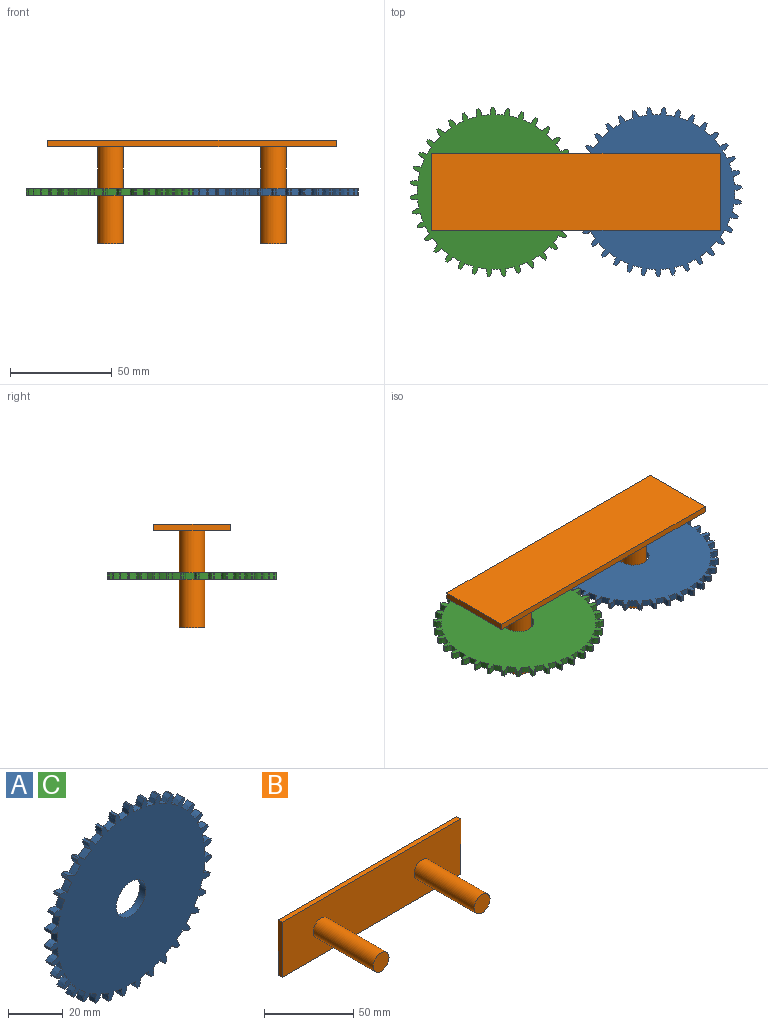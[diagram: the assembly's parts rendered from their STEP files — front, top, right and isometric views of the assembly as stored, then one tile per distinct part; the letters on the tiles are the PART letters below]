
ASSEMBLY  parts=3 mates=2
PART A: 143 faces, bbox 83.3x3.2x83.2 mm
  f0: cylinder r=38.1mm len=4.18mm, axis (0,1,0), area 13.4mm2, adj f1,f139,f140,f141
  f1: extruded ~3.64x3.18mm, area 11.9mm2, adj f0,f2,f140,f141
  f2: plane 3.18x0.92mm, normal (1,0,-0.04), area 2.9mm2, adj f1,f3,f140,f141
  f3: extruded ~3.57x3.18mm, area 11.9mm2, adj f2,f4,f140,f141
  f4: cylinder r=38.1mm len=4.22mm, axis (0,1,0), area 13.4mm2, adj f3,f5,f140,f141
  f5: extruded ~3.46x3.18mm, area 11.9mm2, adj f4,f6,f140,f141
  f6: plane 3.18x0.91mm, normal (0.99,0,0.13), area 2.9mm2, adj f5,f7,f140,f141
  f7: extruded ~3.69x3.18mm, area 11.9mm2, adj f6,f8,f140,f141
  f8: cylinder r=38.1mm len=4.11mm, axis (0,1,0), area 13.4mm2, adj f7,f9,f140,f141
  f9: extruded ~3.18x3.17mm, area 11.9mm2, adj f8,f10,f140,f141
  f10: plane 3.18x0.88mm, normal (0.95,0,0.31), area 2.9mm2, adj f9,f11,f140,f141
  f11: extruded ~3.69x3.18mm, area 11.9mm2, adj f10,f12,f140,f141
  f12: cylinder r=38.1mm len=3.88mm, axis (0,1,0), area 13.4mm2, adj f11,f13,f140,f141
  f13: extruded ~3.18x2.78mm, area 11.9mm2, adj f12,f14,f140,f141
  f14: plane 3.18x0.81mm, normal (0.88,0,0.47), area 2.9mm2, adj f13,f15,f140,f141
  f15: extruded ~3.58x3.18mm, area 11.9mm2, adj f14,f16,f140,f141
  f16: cylinder r=38.1mm len=3.52mm, axis (0,1,0), area 13.4mm2, adj f15,f17,f140,f141
  f17: extruded ~3.18x2.91mm, area 11.9mm2, adj f16,f18,f140,f141
  f18: plane 3.18x0.72mm, normal (0.78,0,0.62), area 2.9mm2, adj f17,f19,f140,f141
  f19: extruded ~3.35x3.18mm, area 11.9mm2, adj f18,f20,f140,f141
  f20: cylinder r=38.1mm len=3.18mm, axis (0,1,0), area 13.4mm2, adj f19,f21,f140,f141
  f21: extruded ~3.28x3.18mm, area 11.9mm2, adj f20,f22,f140,f141
  f22: plane 3.18x0.69mm, normal (0.66,0,0.75), area 2.9mm2, adj f21,f23,f140,f141
  f23: extruded ~3.18x3.01mm, area 11.9mm2, adj f22,f24,f140,f141
  f24: cylinder r=38.1mm len=3.41mm, axis (0,1,0), area 13.4mm2, adj f23,f25,f140,f141
  f25: extruded ~3.53x3.18mm, area 11.9mm2, adj f24,f26,f140,f141
  f26: plane 3.18x0.79mm, normal (0.51,0,0.86), area 2.9mm2, adj f25,f27,f140,f141
  f27: extruded ~3.18x2.66mm, area 11.9mm2, adj f26,f28,f140,f141
  f28: cylinder r=38.1mm len=3.8mm, axis (0,1,0), area 13.4mm2, adj f27,f29,f140,f141
  f29: extruded ~3.68x3.18mm, area 11.9mm2, adj f28,f30,f140,f141
  f30: plane 3.18x0.86mm, normal (0.35,0,0.94), area 2.9mm2, adj f29,f31,f140,f141
  f31: extruded ~3.18x3.08mm, area 11.9mm2, adj f30,f32,f140,f141
  f32: cylinder r=38.1mm len=4.07mm, axis (0,1,0), area 13.4mm2, adj f31,f33,f140,f141
  f33: extruded ~3.7x3.18mm, area 11.9mm2, adj f32,f34,f140,f141
  f34: plane 3.18x0.91mm, normal (0.18,0,0.98), area 2.9mm2, adj f33,f35,f140,f141
  f35: extruded ~3.4x3.18mm, area 11.9mm2, adj f34,f36,f140,f141
  f36: cylinder r=38.1mm len=4.2mm, axis (0,1,0), area 13.4mm2, adj f35,f37,f140,f141
  f37: extruded ~3.61x3.18mm, area 11.9mm2, adj f36,f38,f140,f141
  f38: plane 3.18x0.92mm, normal (0,0,1), area 2.9mm2, adj f37,f39,f140,f141
  f39: extruded ~3.61x3.18mm, area 11.9mm2, adj f38,f40,f140,f141
  f40: cylinder r=38.1mm len=4.2mm, axis (0,1,0), area 13.4mm2, adj f39,f41,f140,f141
  f41: extruded ~3.4x3.18mm, area 11.9mm2, adj f40,f42,f140,f141
  f42: plane 3.18x0.91mm, normal (-0.18,0,0.98), area 2.9mm2, adj f41,f43,f140,f141
  f43: extruded ~3.7x3.18mm, area 11.9mm2, adj f42,f44,f140,f141
  f44: cylinder r=38.1mm len=4.07mm, axis (0,1,0), area 13.4mm2, adj f43,f45,f140,f141
  f45: extruded ~3.18x3.08mm, area 11.9mm2, adj f44,f46,f140,f141
  f46: plane 3.18x0.86mm, normal (-0.35,0,0.94), area 2.9mm2, adj f45,f47,f140,f141
  f47: extruded ~3.68x3.18mm, area 11.9mm2, adj f46,f48,f140,f141
  f48: cylinder r=38.1mm len=3.8mm, axis (0,1,0), area 13.4mm2, adj f47,f49,f140,f141
  f49: extruded ~3.18x2.66mm, area 11.9mm2, adj f48,f50,f140,f141
  f50: plane 3.18x0.79mm, normal (-0.51,0,0.86), area 2.9mm2, adj f49,f51,f140,f141
  f51: extruded ~3.53x3.18mm, area 11.9mm2, adj f50,f52,f140,f141
  f52: cylinder r=38.1mm len=3.41mm, axis (0,1,0), area 13.4mm2, adj f51,f53,f140,f141
  f53: extruded ~3.18x3.01mm, area 11.9mm2, adj f52,f54,f140,f141
  f54: plane 3.18x0.69mm, normal (-0.66,0,0.75), area 2.9mm2, adj f53,f55,f140,f141
  f55: extruded ~3.28x3.18mm, area 11.9mm2, adj f54,f56,f140,f141
  f56: cylinder r=38.1mm len=3.18mm, axis (0,1,0), area 13.4mm2, adj f55,f57,f140,f141
  f57: extruded ~3.35x3.18mm, area 11.9mm2, adj f56,f58,f140,f141
  f58: plane 3.18x0.72mm, normal (-0.78,0,0.62), area 2.9mm2, adj f57,f59,f140,f141
  f59: extruded ~3.18x2.91mm, area 11.9mm2, adj f58,f60,f140,f141
  f60: cylinder r=38.1mm len=3.52mm, axis (0,1,0), area 13.4mm2, adj f59,f61,f140,f141
  f61: extruded ~3.58x3.18mm, area 11.9mm2, adj f60,f62,f140,f141
  f62: plane 3.18x0.81mm, normal (-0.88,0,0.47), area 2.9mm2, adj f61,f63,f140,f141
  f63: extruded ~3.18x2.78mm, area 11.9mm2, adj f62,f64,f140,f141
  f64: cylinder r=38.1mm len=3.88mm, axis (0,1,0), area 13.4mm2, adj f63,f65,f140,f141
  f65: extruded ~3.69x3.18mm, area 11.9mm2, adj f64,f66,f140,f141
  f66: plane 3.18x0.88mm, normal (-0.95,0,0.31), area 2.9mm2, adj f65,f67,f140,f141
  f67: extruded ~3.18x3.17mm, area 11.9mm2, adj f66,f68,f140,f141
  f68: cylinder r=38.1mm len=4.11mm, axis (0,1,0), area 13.4mm2, adj f67,f69,f140,f141
  f69: extruded ~3.69x3.18mm, area 11.9mm2, adj f68,f70,f140,f141
  f70: plane 3.18x0.91mm, normal (-0.99,0,0.13), area 2.9mm2, adj f69,f71,f140,f141
  f71: extruded ~3.46x3.18mm, area 11.9mm2, adj f70,f72,f140,f141
  f72: cylinder r=38.1mm len=4.22mm, axis (0,1,0), area 13.4mm2, adj f71,f73,f140,f141
  f73: extruded ~3.57x3.18mm, area 11.9mm2, adj f72,f74,f140,f141
  f74: plane 3.18x0.92mm, normal (-1,0,-0.04), area 2.9mm2, adj f73,f75,f140,f141
  f75: extruded ~3.64x3.18mm, area 11.9mm2, adj f74,f76,f140,f141
  f76: cylinder r=38.1mm len=4.18mm, axis (0,1,0), area 13.4mm2, adj f75,f77,f140,f141
  f77: extruded ~3.33x3.18mm, area 11.9mm2, adj f76,f78,f140,f141
  f78: plane 3.18x0.9mm, normal (-0.97,0,-0.22), area 2.9mm2, adj f77,f79,f140,f141
  f79: extruded ~3.71x3.18mm, area 11.9mm2, adj f78,f80,f140,f141
  f80: cylinder r=38.1mm len=4.01mm, axis (0,1,0), area 13.4mm2, adj f79,f81,f140,f141
  f81: extruded ~3.18x2.99mm, area 11.9mm2, adj f80,f82,f140,f141
  f82: plane 3.18x0.85mm, normal (-0.92,0,-0.39), area 2.9mm2, adj f81,f83,f140,f141
  f83: extruded ~3.65x3.18mm, area 11.9mm2, adj f82,f84,f140,f141
  f84: cylinder r=38.1mm len=3.72mm, axis (0,1,0), area 13.4mm2, adj f83,f85,f140,f141
  f85: extruded ~3.18x2.7mm, area 11.9mm2, adj f84,f86,f140,f141
  f86: plane 3.18x0.77mm, normal (-0.83,0,-0.55), area 2.9mm2, adj f85,f87,f140,f141
  f87: extruded ~3.48x3.18mm, area 11.9mm2, adj f86,f88,f140,f141
  f88: cylinder r=38.1mm len=3.3mm, axis (0,1,0), area 13.4mm2, adj f87,f89,f140,f141
  f89: extruded ~3.18x3.11mm, area 11.9mm2, adj f88,f90,f140,f141
  f90: plane 3.18x0.67mm, normal (-0.72,0,-0.69), area 2.9mm2, adj f89,f91,f140,f141
  f91: extruded ~3.19x3.18mm, area 11.9mm2, adj f90,f92,f140,f141
  f92: cylinder r=38.1mm len=3.18mm, axis (0,1,0), area 13.4mm2, adj f91,f93,f140,f141
  f93: extruded ~3.42x3.18mm, area 11.9mm2, adj f92,f94,f140,f141
  f94: plane 3.18x0.75mm, normal (-0.59,0,-0.81), area 2.9mm2, adj f93,f95,f140,f141
  f95: extruded ~3.18x2.81mm, area 11.9mm2, adj f94,f96,f140,f141
  f96: cylinder r=38.1mm len=3.62mm, axis (0,1,0), area 13.4mm2, adj f95,f97,f140,f141
  f97: extruded ~3.62x3.18mm, area 11.9mm2, adj f96,f98,f140,f141
  f98: plane 3.18x0.83mm, normal (-0.43,0,-0.9), area 2.9mm2, adj f97,f99,f140,f141
  f99: extruded ~3.18x2.88mm, area 11.9mm2, adj f98,f100,f140,f141
  f100: cylinder r=38.1mm len=3.95mm, axis (0,1,0), area 13.4mm2, adj f99,f101,f140,f141
  f101: extruded ~3.7x3.18mm, area 11.9mm2, adj f100,f102,f140,f141
  f102: plane 3.18x0.89mm, normal (-0.27,0,-0.96), area 2.9mm2, adj f101,f103,f140,f141
  f103: extruded ~3.25x3.18mm, area 11.9mm2, adj f102,f104,f140,f141
  f104: cylinder r=38.1mm len=4.15mm, axis (0,1,0), area 13.4mm2, adj f103,f105,f140,f141
  f105: extruded ~3.67x3.18mm, area 11.9mm2, adj f104,f106,f140,f141
  f106: plane 3.18x0.92mm, normal (-0.09,0,-1), area 2.9mm2, adj f105,f107,f140,f141
  f107: extruded ~3.52x3.18mm, area 11.9mm2, adj f106,f108,f140,f141
  f108: cylinder r=38.1mm len=4.22mm, axis (0,1,0), area 13.4mm2, adj f107,f109,f140,f141
  f109: extruded ~3.52x3.18mm, area 11.9mm2, adj f108,f110,f140,f141
  f110: plane 3.18x0.92mm, normal (0.09,0,-1), area 2.9mm2, adj f109,f111,f140,f141
  f111: extruded ~3.67x3.18mm, area 11.9mm2, adj f110,f112,f140,f141
  f112: cylinder r=38.1mm len=4.15mm, axis (0,1,0), area 13.4mm2, adj f111,f113,f140,f141
  f113: extruded ~3.25x3.18mm, area 11.9mm2, adj f112,f114,f140,f141
  f114: plane 3.18x0.89mm, normal (0.27,0,-0.96), area 2.9mm2, adj f113,f115,f140,f141
  f115: extruded ~3.7x3.18mm, area 11.9mm2, adj f114,f116,f140,f141
  f116: cylinder r=38.1mm len=3.95mm, axis (0,1,0), area 13.4mm2, adj f115,f117,f140,f141
  f117: extruded ~3.18x2.88mm, area 11.9mm2, adj f116,f118,f140,f141
  f118: plane 3.18x0.83mm, normal (0.43,0,-0.9), area 2.9mm2, adj f117,f119,f140,f141
  f119: extruded ~3.62x3.18mm, area 11.9mm2, adj f118,f120,f140,f141
  f120: cylinder r=38.1mm len=3.62mm, axis (0,1,0), area 13.4mm2, adj f119,f121,f140,f141
  f121: extruded ~3.18x2.81mm, area 11.9mm2, adj f120,f122,f140,f141
  f122: plane 3.18x0.75mm, normal (0.59,0,-0.81), area 2.9mm2, adj f121,f123,f140,f141
  f123: extruded ~3.42x3.18mm, area 11.9mm2, adj f122,f124,f140,f141
  f124: cylinder r=38.1mm len=3.18mm, axis (0,1,0), area 13.4mm2, adj f123,f125,f140,f141
  f125: extruded ~3.19x3.18mm, area 11.9mm2, adj f124,f126,f140,f141
  f126: plane 3.18x0.67mm, normal (0.72,0,-0.69), area 2.9mm2, adj f125,f127,f140,f141
  f127: extruded ~3.18x3.11mm, area 11.9mm2, adj f126,f128,f140,f141
  f128: cylinder r=38.1mm len=3.3mm, axis (0,1,0), area 13.4mm2, adj f127,f129,f140,f141
  f129: extruded ~3.48x3.18mm, area 11.9mm2, adj f128,f130,f140,f141
  f130: plane 3.18x0.77mm, normal (0.83,0,-0.55), area 2.9mm2, adj f129,f131,f140,f141
  f131: extruded ~3.18x2.7mm, area 11.9mm2, adj f130,f132,f140,f141
  f132: cylinder r=38.1mm len=3.72mm, axis (0,1,0), area 13.4mm2, adj f131,f133,f140,f141
  f133: extruded ~3.65x3.18mm, area 11.9mm2, adj f132,f134,f140,f141
  f134: plane 3.18x0.85mm, normal (0.92,0,-0.39), area 2.9mm2, adj f133,f135,f140,f141
  f135: extruded ~3.18x2.99mm, area 11.9mm2, adj f134,f136,f140,f141
  f136: cylinder r=38.1mm len=4.01mm, axis (0,1,0), area 13.4mm2, adj f135,f137,f140,f141
  f137: extruded ~3.71x3.18mm, area 11.9mm2, adj f136,f138,f140,f141
  f138: plane 3.18x0.9mm, normal (0.97,0,-0.22), area 2.9mm2, adj f137,f139,f140,f141
  f139: extruded ~3.33x3.18mm, area 11.9mm2, adj f0,f138,f140,f141
  f140: plane 83.33x83.25mm, normal (0,-1,0), area 4648.1mm2, adj f0,f1,f2,f3,f4,f5,f6,f7
  f141: plane 83.33x83.25mm, normal (0,1,0), area 4648.1mm2, adj f0,f1,f2,f3,f4,f5,f6,f7
  f142: cylinder r=7.62mm len=15.24mm, axis (0,1,0), area 152mm2, adj f140,f141
PART B: 10 faces, bbox 141.7x50.8x37.8 mm
  f0: plane 37.84x3.18mm, normal (1,0,0), area 120.1mm2, adj f1,f3,f4,f5
  f1: plane 141.74x3.18mm, normal (0,0,1), area 450mm2, adj f0,f2,f4,f5
  f2: plane 37.84x3.18mm, normal (-1,0,0), area 120.1mm2, adj f1,f3,f4,f5
  f3: plane 141.74x3.18mm, normal (0,0,-1), area 450mm2, adj f0,f2,f4,f5
  f4: plane 141.74x37.84mm, normal (0,-1,0), area 5114.8mm2, adj f0,f1,f2,f3,f6,f8
  f5: plane 141.74x37.84mm, normal (0,1,0), area 5362.8mm2, adj f0,f1,f2,f3
  f6: cylinder r=6.28mm len=47.63mm, axis (0,1,0), area 1880.2mm2, adj f4,f7
  f7: plane 12.57x12.57mm, normal (0,-1,0), area 124mm2, adj f6
  f8: cylinder r=6.28mm len=47.63mm, axis (0,1,0), area 1880.2mm2, adj f4,f9
  f9: plane 12.57x12.57mm, normal (0,-1,0), area 124mm2, adj f8
PART C: same geometry as A
PLACE A rot(axis=(0.1,-0.7,-0.7),168.6deg) t=(37.63,1.29,-23.81)mm
PLACE B rot(axis=(1,0,0),90deg) t=(-2.37,1.29,0)mm fixed
PLACE C rot(axis=(0.06,0.71,0.71),173.6deg) t=(-42.37,1.29,-23.81)mm
MATE revolute C.f142 <-> B.f6  axis (0,0,-1) through (-42.37,1.29,-26.99)mm
MATE revolute A.f142 <-> B.f8  axis (0,0,-1) through (37.63,1.29,-26.99)mm
